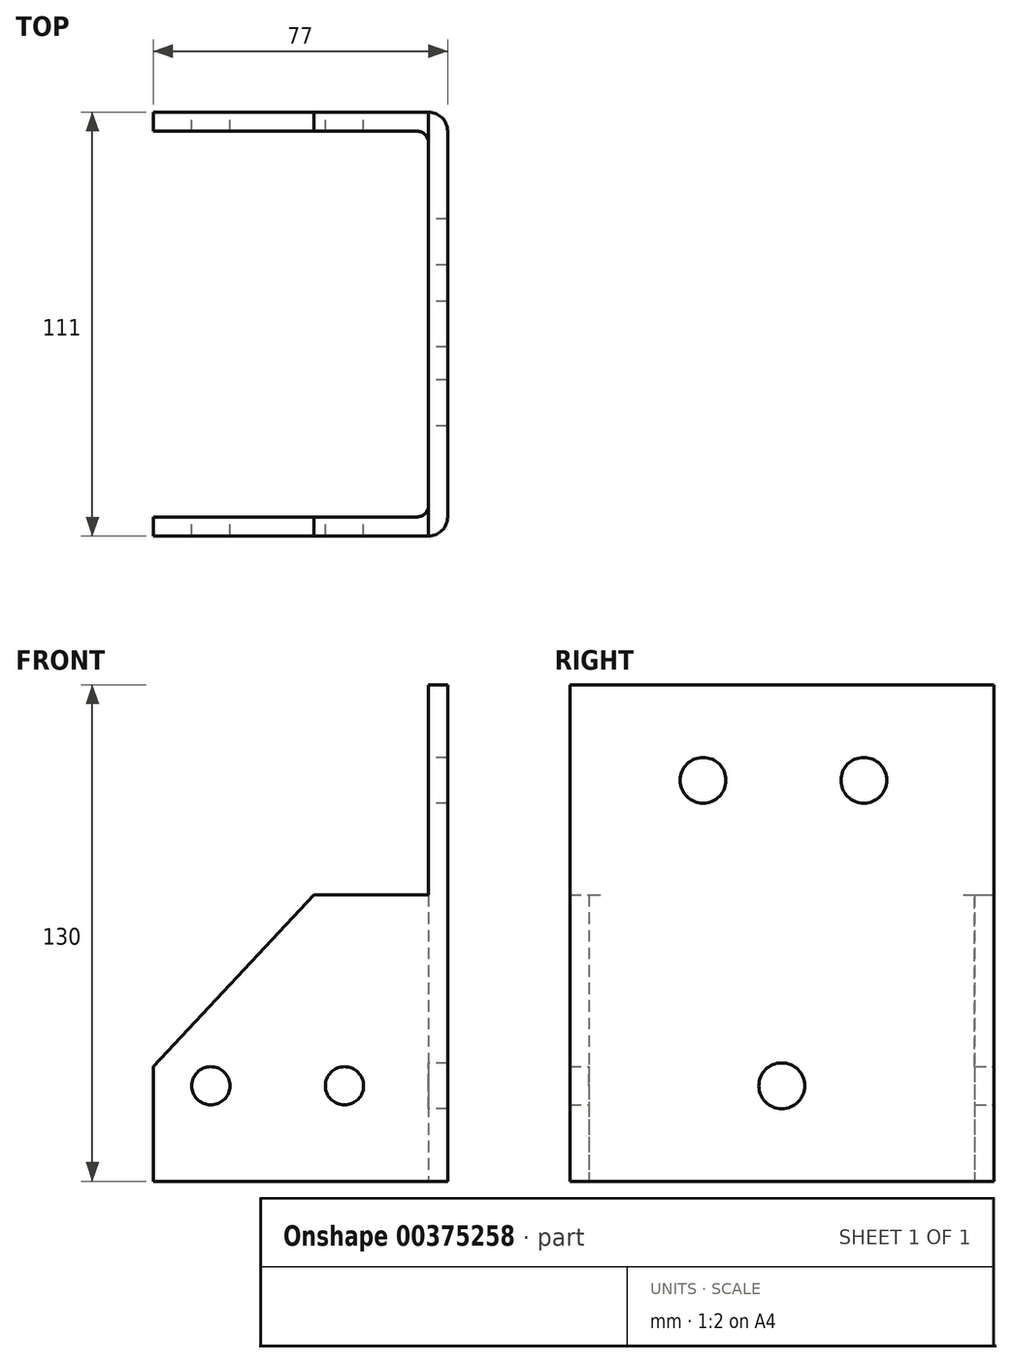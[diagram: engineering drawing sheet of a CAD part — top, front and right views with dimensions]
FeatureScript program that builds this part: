
annotation { "Feature Type Name" : "Feature", "Feature Type Description" : "" }
export const myFeature = defineFeature(function(context is Context, id is Id, definition is map)
    precondition{}
    {
        {
            var Q0;
            Q0=qCreatedBy(makeId("Top.planeOp"),FACE);
            var sketch = newSketch(context, id + "F0", { "sketchPlane" : qUnion([Q0])});
            skLineSegment(sketch, "E0", {"start": v(-54.08, 92) * mm, "end": v(-54.08, 87) * mm});
            skLineSegment(sketch, "E1", {"start": v(-54.08, 87) * mm, "end": v(14.92, 87) * mm});
            skLineSegment(sketch, "E2", {"start": v(17.92, 84) * mm, "end": v(17.92, -11) * mm});
            skLineSegment(sketch, "E3", {"start": v(14.92, -14) * mm, "end": v(-54.08, -14) * mm});
            skLineSegment(sketch, "E4", {"start": v(-54.08, -14) * mm, "end": v(-54.08, -19) * mm});
            skLineSegment(sketch, "E5", {"start": v(-54.08, -19) * mm, "end": v(17.92, -19) * mm});
            skLineSegment(sketch, "E6", {"start": v(22.92, -14) * mm, "end": v(22.92, 87) * mm});
            skLineSegment(sketch, "E7", {"start": v(17.92, 92) * mm, "end": v(-54.08, 92) * mm});
            skPoint(sketch, "E8.visualSharp", {"position": v(22.92, 92) * mm});
            skArc(sketch, "E8.filletArc", {"start": v(22.92, 87) * mm, "mid": v(21.46, 90.54) * mm, "end": v(17.92, 92) * mm});
            skArc(sketch, "E9.filletArc", {"start": v(17.92, 84) * mm, "mid": v(17.04, 86.13) * mm, "end": v(14.92, 87) * mm});
            skPoint(sketch, "E10.visualSharp", {"position": v(17.92, -14) * mm});
            skArc(sketch, "E10.filletArc", {"start": v(14.92, -14) * mm, "mid": v(17.04, -13.11) * mm, "end": v(17.92, -11) * mm});
            skPoint(sketch, "E11.visualSharp", {"position": v(22.92, -19) * mm});
            skArc(sketch, "E11.filletArc", {"start": v(17.92, -19) * mm, "mid": v(21.46, -17.53) * mm, "end": v(22.92, -14) * mm});
            skSolve(sketch);
        }
        {
            var Q0;
            Q0=makeQuery(id+"F0.imprint","IMPRINT",FACE,{"disambiguationData":[TD([[makeQuery(id+"F0.imprint","IMPRINT",EDGE,{"derivedFrom":sQuery(id+"F0.wireOp",EDGE,"E0")}),1.0]])]});
            extrude(context, id + "F1", {"entities" : qUnion([Q0]), "depth" : 130 * mm});
        }
        {
            var Q0;
            Q0=makeQuery(id+"F1.opExtrude","SWEPT_FACE",FACE,{"disambiguationData":[OSD([sQuery(id+"F0.wireOp",EDGE,"E2")])]});
            var sketch = newSketch(context, id + "F2", { "sketchPlane" : qUnion([Q0])});
            skCircle(sketch, "E12", {"center": v(-58, 105) * mm, "radius": 6 * mm});
            skCircle(sketch, "E13", {"center": v(-15.89, 105) * mm, "radius": 6 * mm});
            skCircle(sketch, "E14", {"center": v(-36.5, 25) * mm, "radius": 6 * mm});
            skSolve(sketch);
        }
        {
            var Q0;
            Q0=makeQuery(id+"F2.imprint","IMPRINT",FACE,{"disambiguationData":[TD([[makeQuery(id+"F2.imprint","IMPRINT",EDGE,{"derivedFrom":sQuery(id+"F2.wireOp",EDGE,"E13")}),1.0]])]});
            var Q1;
            Q1=makeQuery(id+"F2.imprint","IMPRINT",FACE,{"disambiguationData":[TD([[makeQuery(id+"F2.imprint","IMPRINT",EDGE,{"derivedFrom":sQuery(id+"F2.wireOp",EDGE,"E14")}),1.0]])]});
            var Q2;
            Q2=makeQuery(id+"F2.imprint","IMPRINT",FACE,{"disambiguationData":[TD([[makeQuery(id+"F2.imprint","IMPRINT",EDGE,{"derivedFrom":sQuery(id+"F2.wireOp",EDGE,"E12")}),1.0]])]});
            extrude(context, id + "F3", {"entities" : qUnion([Q0, Q1, Q2]), "operationType" : NewBodyOperationType.REMOVE, "endBound" : BoundingType.THROUGH_ALL, "oppositeDirection" : true, "depth" : 25 * mm});
        }
        {
            var Q0;
            Q0=makeQuery(id+"F1.opExtrude","SWEPT_FACE",FACE,{"disambiguationData":[OSD([sQuery(id+"F0.wireOp",EDGE,"E7")])]});
            var sketch = newSketch(context, id + "F4", { "sketchPlane" : qUnion([Q0])});
            skCircle(sketch, "E15", {"center": v(39.08, 25) * mm, "radius": 5 * mm});
            skCircle(sketch, "E16", {"center": v(4.08, 25) * mm, "radius": 5 * mm});
            skLineSegment(sketch, "E17", {"start": v(54.08, 30) * mm, "end": v(12.08, 75) * mm});
            skLineSegment(sketch, "E18", {"start": v(12.08, 75) * mm, "end": v(-17.92, 75) * mm});
            skSolve(sketch);
        }
        {
            var Q0;
            Q0 = qSketchRegion(id + "F4", true);
            var Q1;
            {var subQ4=sQuery(id+"F4.wireOp",EDGE,"E17");Q1=makeQuery(id+"F4.imprint","IMPRINT",FACE,{"disambiguationData":[TD([[makeQuery(id+"F4.imprint","IMPRINT",EDGE,{"derivedFrom":subQ4}),-1.0]])]});}
            extrude(context, id + "F5", {"entities" : qUnion([Q0, Q1]), "operationType" : NewBodyOperationType.REMOVE, "endBound" : BoundingType.THROUGH_ALL, "oppositeDirection" : true, "depth" : 25 * mm});
        }
    });
